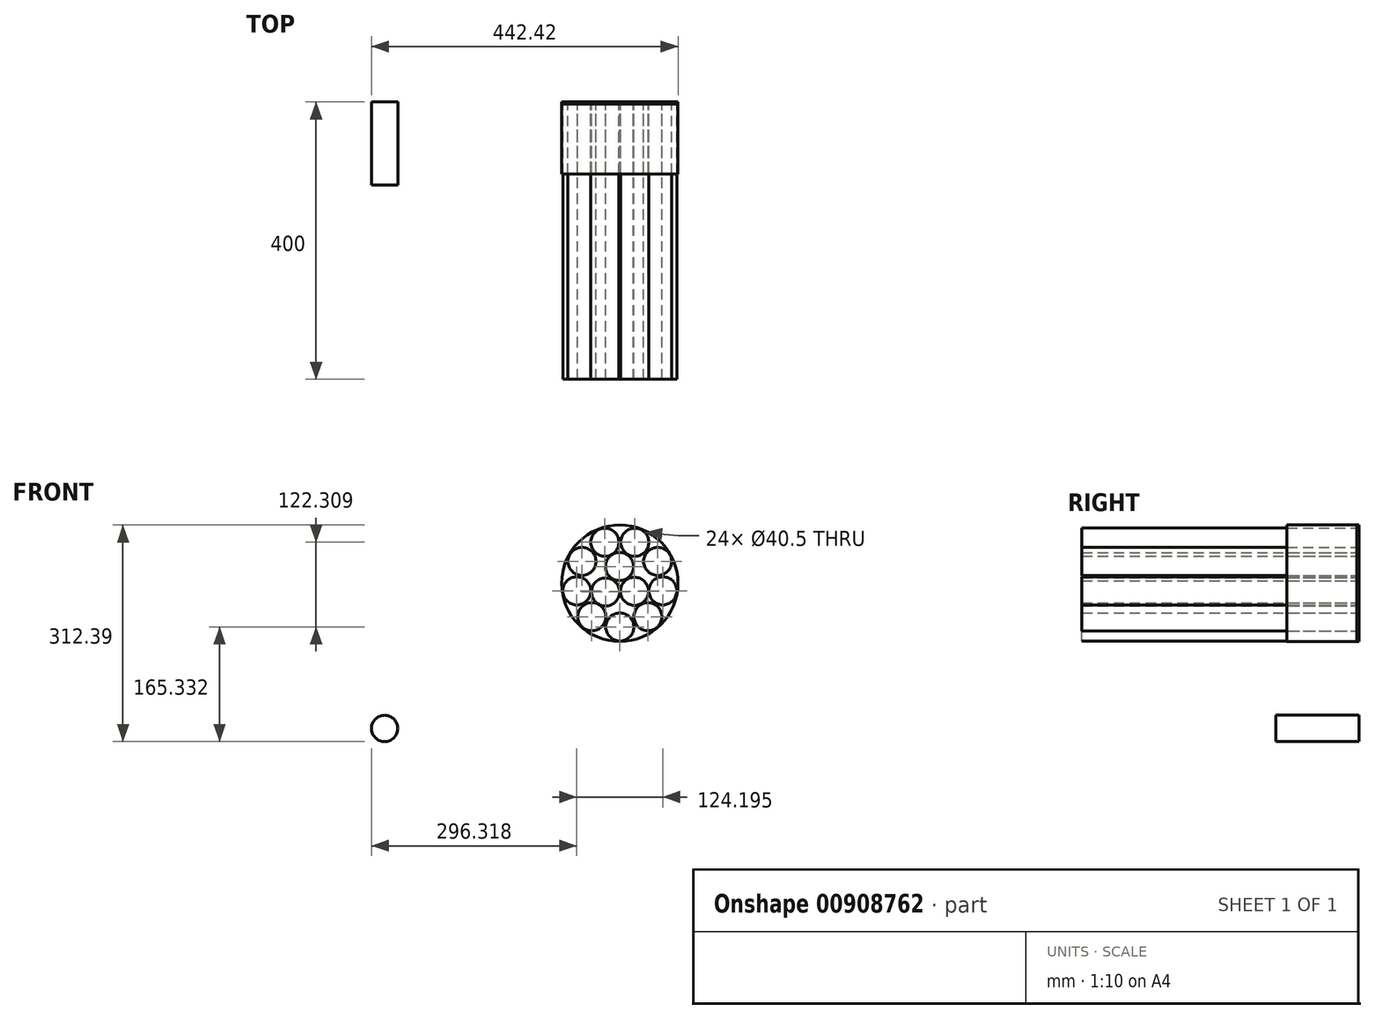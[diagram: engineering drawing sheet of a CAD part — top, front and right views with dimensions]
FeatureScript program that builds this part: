
annotation { "Feature Type Name" : "Feature", "Feature Type Description" : "" }
export const myFeature = defineFeature(function(context is Context, id is Id, definition is map)
    precondition{}
    {
        {
            var Q0;
            Q0=qCreatedBy(makeId("Front.planeOp"),FACE);
            var sketch = newSketch(context, id + "F0", { "sketchPlane" : qUnion([Q0])});
            skCircle(sketch, "E0", {"center": v(-151.31, -29.12) * mm, "radius": 19 * mm});
            skCircle(sketch, "E1", {"center": v(188.1, 180.27) * mm, "radius": 84 * mm});
            skCircle(sketch, "E2", {"center": v(188.1, 117.21) * mm, "radius": 20.25 * mm});
            skCircle(sketch, "E3.1.0", {"center": v(228.64, 131.96) * mm, "radius": 20.25 * mm});
            skCircle(sketch, "E3.2.0", {"center": v(250.2, 169.32) * mm, "radius": 20.25 * mm});
            skCircle(sketch, "E3.3.0", {"center": v(242.71, 211.8) * mm, "radius": 20.25 * mm});
            skCircle(sketch, "E3.4.0", {"center": v(209.67, 239.52) * mm, "radius": 20.25 * mm});
            skCircle(sketch, "E3.5.0", {"center": v(166.54, 239.52) * mm, "radius": 20.25 * mm});
            skCircle(sketch, "E3.6.0", {"center": v(133.5, 211.8) * mm, "radius": 20.25 * mm});
            skCircle(sketch, "E3.7.0", {"center": v(126, 169.32) * mm, "radius": 20.25 * mm});
            skCircle(sketch, "E3.8.0", {"center": v(147.57, 131.96) * mm, "radius": 20.25 * mm});
            skCircle(sketch, "E4", {"center": v(209.2, 168.68) * mm, "radius": 20.25 * mm});
            skCircle(sketch, "E5.1.0", {"center": v(187.6, 204.34) * mm, "radius": 20.25 * mm});
            skCircle(sketch, "E5.2.0", {"center": v(167.52, 167.79) * mm, "radius": 20.25 * mm});
            skSolve(sketch);
        }
        {
            var Q0;
            Q0=makeQuery(id+"F0.imprint","IMPRINT",FACE,{"disambiguationData":[TD([[makeQuery(id+"F0.imprint","IMPRINT",EDGE,{"derivedFrom":sQuery(id+"F0.wireOp",EDGE,"E1")}),1.0]])]});
            extrude(context, id + "F1", {"entities" : qUnion([Q0]), "depth" : 3 * mm, "offsetDistance" : 25 * mm});
        }
        {
            var Q0;
            Q0=makeQuery(id+"F0.imprint","IMPRINT",FACE,{"disambiguationData":[TD([[makeQuery(id+"F0.imprint","IMPRINT",EDGE,{"derivedFrom":sQuery(id+"F0.wireOp",EDGE,"E0")}),1.0]])]});
            extrude(context, id + "F2", {"entities" : qUnion([Q0]), "depth" : 120 * mm, "offsetDistance" : 25 * mm});
        }
        {
            var Q0;
            Q0=makeQuery(id+"F0.imprint","IMPRINT",FACE,{"disambiguationData":[TD([[makeQuery(id+"F0.imprint","IMPRINT",EDGE,{"derivedFrom":sQuery(id+"F0.wireOp",EDGE,"E1")}),1.0]])]});
            extrude(context, id + "F3", {"entities" : qUnion([Q0]), "depth" : 104 * mm, "offsetDistance" : 25 * mm});
        }
        {
            var Q0;
            Q0=makeQuery(id+"F0.imprint","IMPRINT",FACE,{"disambiguationData":[TD([[makeQuery(id+"F0.imprint","IMPRINT",EDGE,{"derivedFrom":sQuery(id+"F0.wireOp",EDGE,"E3.6.0")}),1.0]])]});
            var Q1;
            Q1=makeQuery(id+"F0.imprint","IMPRINT",FACE,{"disambiguationData":[TD([[makeQuery(id+"F0.imprint","IMPRINT",EDGE,{"derivedFrom":sQuery(id+"F0.wireOp",EDGE,"E3.5.0")}),1.0]])]});
            var Q2;
            Q2=makeQuery(id+"F0.imprint","IMPRINT",FACE,{"disambiguationData":[TD([[makeQuery(id+"F0.imprint","IMPRINT",EDGE,{"derivedFrom":sQuery(id+"F0.wireOp",EDGE,"E3.4.0")}),1.0]])]});
            var Q3;
            Q3=makeQuery(id+"F0.imprint","IMPRINT",FACE,{"disambiguationData":[TD([[makeQuery(id+"F0.imprint","IMPRINT",EDGE,{"derivedFrom":sQuery(id+"F0.wireOp",EDGE,"E5.1.0")}),1.0]])]});
            var Q4;
            Q4=makeQuery(id+"F0.imprint","IMPRINT",FACE,{"disambiguationData":[TD([[makeQuery(id+"F0.imprint","IMPRINT",EDGE,{"derivedFrom":sQuery(id+"F0.wireOp",EDGE,"E4")}),1.0]])]});
            var Q5;
            Q5=makeQuery(id+"F0.imprint","IMPRINT",FACE,{"disambiguationData":[TD([[makeQuery(id+"F0.imprint","IMPRINT",EDGE,{"derivedFrom":sQuery(id+"F0.wireOp",EDGE,"E5.2.0")}),1.0]])]});
            var Q6;
            Q6=makeQuery(id+"F0.imprint","IMPRINT",FACE,{"disambiguationData":[TD([[makeQuery(id+"F0.imprint","IMPRINT",EDGE,{"derivedFrom":sQuery(id+"F0.wireOp",EDGE,"E3.7.0")}),1.0]])]});
            var Q7;
            Q7=makeQuery(id+"F0.imprint","IMPRINT",FACE,{"disambiguationData":[TD([[makeQuery(id+"F0.imprint","IMPRINT",EDGE,{"derivedFrom":sQuery(id+"F0.wireOp",EDGE,"E3.8.0")}),1.0]])]});
            var Q8;
            Q8=makeQuery(id+"F0.imprint","IMPRINT",FACE,{"disambiguationData":[TD([[makeQuery(id+"F0.imprint","IMPRINT",EDGE,{"derivedFrom":sQuery(id+"F0.wireOp",EDGE,"E2")}),1.0]])]});
            var Q9;
            Q9=makeQuery(id+"F0.imprint","IMPRINT",FACE,{"disambiguationData":[TD([[makeQuery(id+"F0.imprint","IMPRINT",EDGE,{"derivedFrom":sQuery(id+"F0.wireOp",EDGE,"E3.1.0")}),1.0]])]});
            var Q10;
            Q10=makeQuery(id+"F0.imprint","IMPRINT",FACE,{"disambiguationData":[TD([[makeQuery(id+"F0.imprint","IMPRINT",EDGE,{"derivedFrom":sQuery(id+"F0.wireOp",EDGE,"E3.2.0")}),1.0]])]});
            var Q11;
            Q11=makeQuery(id+"F0.imprint","IMPRINT",FACE,{"disambiguationData":[TD([[makeQuery(id+"F0.imprint","IMPRINT",EDGE,{"derivedFrom":sQuery(id+"F0.wireOp",EDGE,"E3.3.0")}),1.0]])]});
            extrude(context, id + "F5", {"entities" : qUnion([Q0, Q1, Q2, Q3, Q4, Q5, Q6, Q7, Q8, Q9, Q10, Q11]), "depth" : 400 * mm, "offsetDistance" : 25 * mm});
        }
    });
